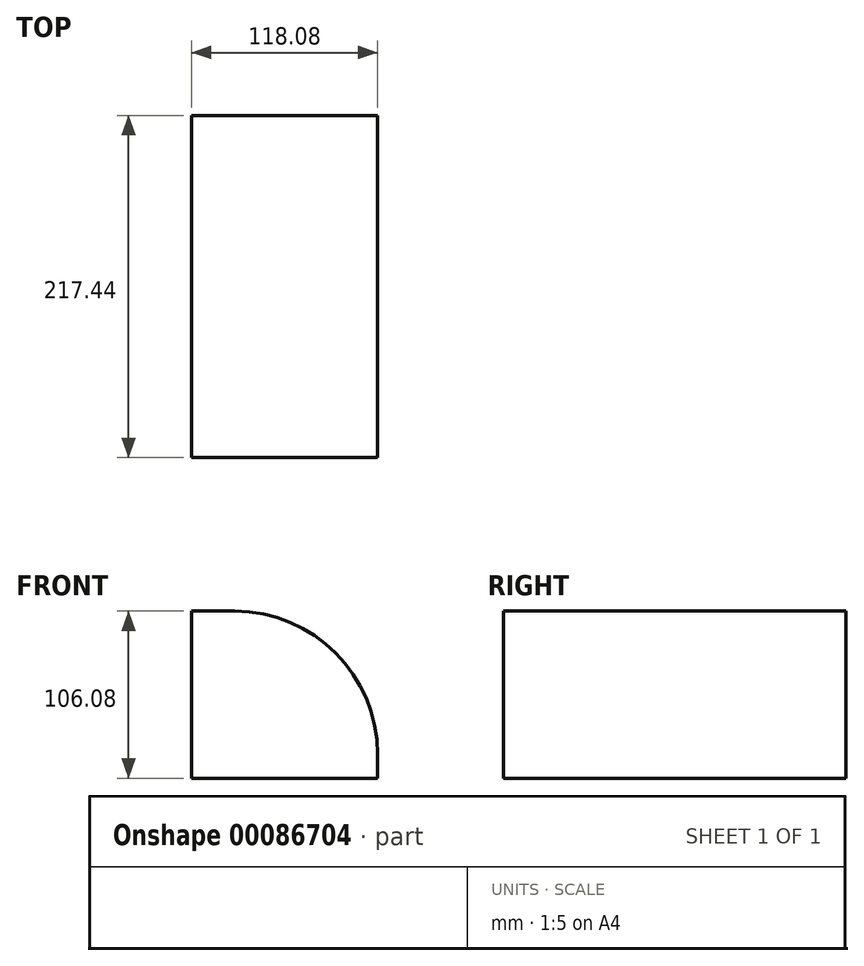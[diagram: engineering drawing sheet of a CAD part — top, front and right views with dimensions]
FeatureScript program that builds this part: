
annotation { "Feature Type Name" : "Feature", "Feature Type Description" : "" }
export const myFeature = defineFeature(function(context is Context, id is Id, definition is map)
    precondition{}
    {
        {
            var Q0;
            Q0=qCreatedBy(makeId("Top.planeOp"),FACE);
            var sketch = newSketch(context, id + "F2", { "sketchPlane" : qUnion([Q0])});
            skLineSegment(sketch, "E0.bottom", {"start": v(-59.04, 108.72) * mm, "end": v(59.04, 108.72) * mm});
            skLineSegment(sketch, "E0.top", {"start": v(-59.04, -108.72) * mm, "end": v(59.04, -108.72) * mm});
            skLineSegment(sketch, "E0.left", {"start": v(-59.04, 108.72) * mm, "end": v(-59.04, -108.72) * mm});
            skLineSegment(sketch, "E0.right", {"start": v(59.04, 108.72) * mm, "end": v(59.04, -108.72) * mm});
            skPoint(sketch, "E0.middle", {"position": v(0, 0) * mm});
            skSolve(sketch);
        }
        {
            var Q0;
            Q0=makeQuery(id+"F2.imprint","IMPRINT",FACE,{"disambiguationData":[TD([[makeQuery(id+"F2.imprint","IMPRINT",EDGE,{"derivedFrom":sQuery(id+"F2.wireOp",EDGE,"E0.bottom")}),-1.0]])]});
            extrude(context, id + "F0", {"entities" : qUnion([Q0]), "depth" : 106.08 * mm});
        }
        {
            var Q0;
            Q0=makeQuery(id+"F0.opExtrude","CAP_EDGE",EDGE,{"disambiguationData":[OSD([sQuery(id+"F2.wireOp",EDGE,"E0.right")])],"isStart":false});
            fillet(context, id + "F1", {"entities" : qUnion([Q0]), "radius" : 90.85 * mm, "tangentPropagation" : true, "allowEdgeOverflow" : false});
        }
    });
